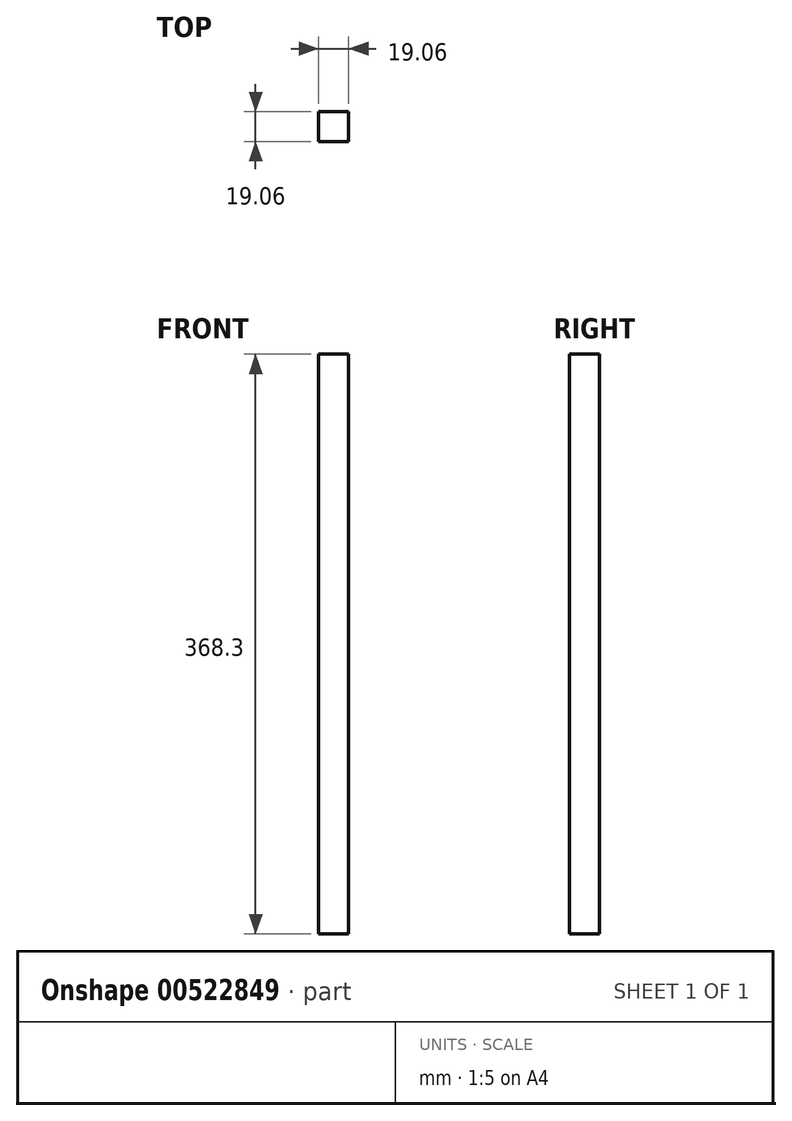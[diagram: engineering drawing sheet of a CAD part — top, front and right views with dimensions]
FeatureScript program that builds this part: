
annotation { "Feature Type Name" : "Feature", "Feature Type Description" : "" }
export const myFeature = defineFeature(function(context is Context, id is Id, definition is map)
    precondition{}
    {
        {
            var Q0;
            Q0=qCreatedBy(makeId("Top.planeOp"),FACE);
            var sketch = newSketch(context, id + "F0", { "sketchPlane" : qUnion([Q0])});
            skLineSegment(sketch, "E0.bottom", {"start": v(-9.53, 9.53) * mm, "end": v(9.53, 9.53) * mm});
            skLineSegment(sketch, "E0.top", {"start": v(-9.53, -9.52) * mm, "end": v(9.52, -9.52) * mm});
            skLineSegment(sketch, "E0.left", {"start": v(-9.52, 9.53) * mm, "end": v(-9.53, -9.52) * mm});
            skLineSegment(sketch, "E0.right", {"start": v(9.53, 9.53) * mm, "end": v(9.53, -9.52) * mm});
            skPoint(sketch, "E0.middle", {"position": v(0, 0) * mm});
            skSolve(sketch);
        }
        {
            var Q0;
            Q0 = qSketchRegion(id + "F0", true);
            extrude(context, id + "F1", {"entities" : qUnion([Q0]), "depth" : 368.3 * mm, "offsetDistance" : 25.4 * mm});
        }
    });
